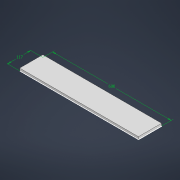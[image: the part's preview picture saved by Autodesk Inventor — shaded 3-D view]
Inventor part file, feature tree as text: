
AUTODESK INVENTOR PART (.ipt)
format: ipt  version: 2022 (Build 260153000, 153)  size: 88,064 bytes
history: native  units: mm
features: other x1, extrude x1, sketch x1
ambient origin geometry x8: Origin, YZ Plane, XZ Plane, XY Plane, X Axis, Y Axis, Z Axis, Center Point
bodies: Body1 (feature_tree)
feature tree (3):
  other  "Твердое тело1"
  extrude  "Выдавливание1"  Depth=600.0mm
  sketch  "Эскиз1"
